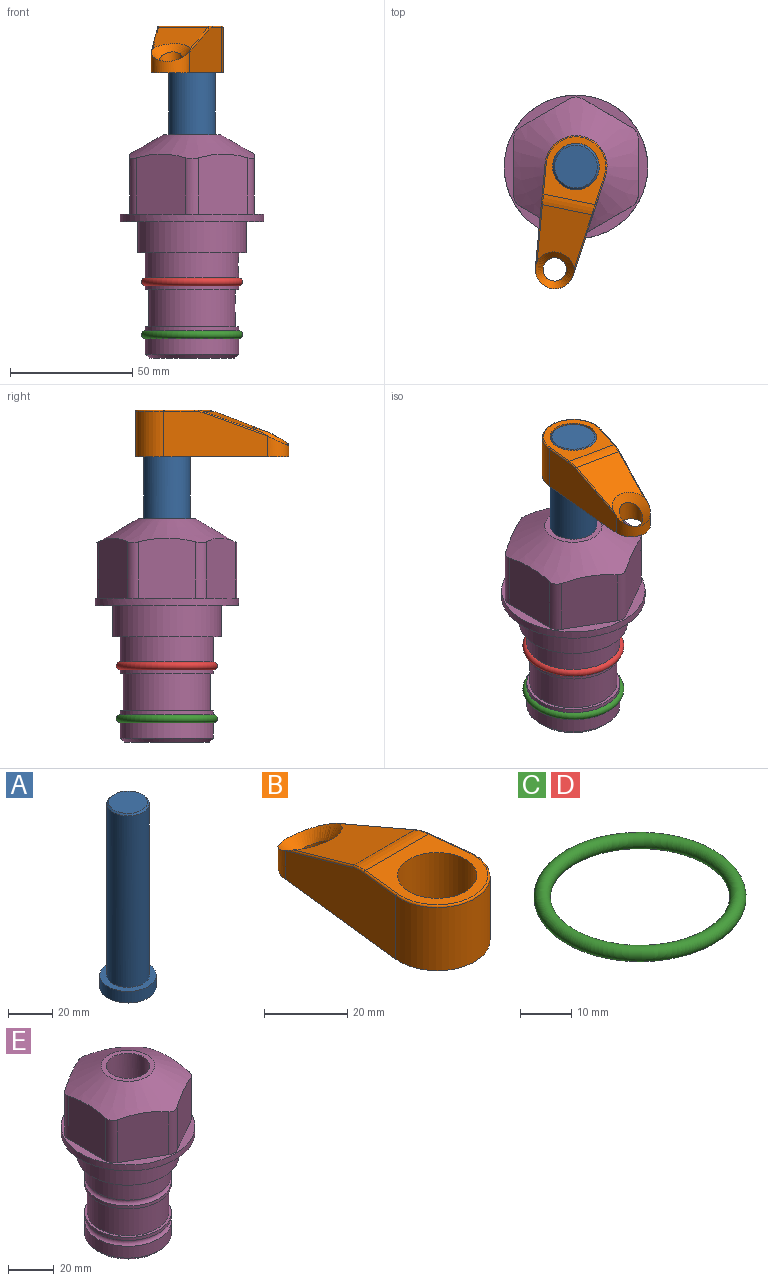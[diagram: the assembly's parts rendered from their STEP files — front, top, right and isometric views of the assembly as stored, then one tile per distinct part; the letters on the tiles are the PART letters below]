
ASSEMBLY  parts=5 mates=3
PART A: 6 faces, bbox 25.4x25.4x101.6 mm
  f0: plane 17.46x17.46mm, normal (0,0,1), area 239.5mm2, adj f5
  f1: plane 25.4x25.4mm, normal (0,0,-1), area 506.7mm2, adj f2
  f2: cylinder r=12.7mm len=25.4mm, axis (0,0,1), area 506.7mm2, adj f1,f3
  f3: plane 25.4x25.4mm, normal (0,0,1), area 221.7mm2, adj f2,f4
  f4: cylinder r=9.53mm len=94.46mm, axis (0,0,1), area 5653mm2, adj f3,f5
  f5: cone r=8.73mm half-angle=45deg, axis (0,0,-1), area 64.4mm2, adj f0,f4
PART B: 46 faces, bbox 27.5x66.1x19.1 mm
  f0: bspline ~0.38x0.18mm, area 0mm2, adj f5,f19,f45
  f1: plane 2.3x0.95mm, normal (0,0,-1), area 1mm2, adj f26,f31,f35
  f2: plane 63.5x25.4mm, normal (0,0,-1), area 561.7mm2, adj f3,f4,f5,f6,f7,f8,f20,f21
  f3: cylinder r=12.7mm len=25.4mm, axis (0,0,-1), area 792.2mm2, adj f2,f4,f6,f14
  f4: plane 42.33x18.54mm, normal (0.99,0.11,0), area 647mm2, adj f2,f3,f5,f12,f13,f15
  f5: cylinder r=7.94mm len=15.78mm, axis (0,0,-1), area 139.4mm2, adj f0,f2,f4,f6,f17,f45
  f6: plane 42.33x18.54mm, normal (-0.99,0.11,0), area 647mm2, adj f2,f3,f5,f16,f18,f19
  f7: cylinder r=9.53mm len=19.05mm, axis (0,0,-1), area 1140.1mm2, adj f2,f9
  f8: cylinder r=4.76mm len=9.53mm, axis (0,0,-1), area 163mm2, adj f2,f45
  f9: plane 25.83x24.38mm, normal (0,0,1), area 262.2mm2, adj f7,f11,f12,f14,f16
  f10: plane 22.98x20.56mm, normal (0,0.34,0.94), area 378mm2, adj f11,f15,f19,f45
  f11: cylinder r=12.7mm len=21.49mm, axis (-1,0,0), area 93.2mm2, adj f9,f10,f13,f18
  f12: cylinder r=0.51mm len=12.34mm, axis (0.11,-0.99,0), area 9.9mm2, adj f4,f9,f13,f14
  f13: bspline ~7.62x1.64mm, area 3.5mm2, adj f4,f11,f12,f15
  f14: torus R=12.19mm, axis (0,0,1), area 33.6mm2, adj f3,f9,f12,f16
  f15: cylinder r=0.51mm len=26.01mm, axis (0.1,-0.93,0.34), area 20.2mm2, adj f4,f10,f13,f17,f45
  f16: cylinder r=0.51mm len=12.34mm, axis (0.11,0.99,0), area 9.9mm2, adj f6,f9,f14,f18
  f17: bspline ~0.38x0.18mm, area 0mm2, adj f5,f15,f45
  f18: bspline ~7.62x1.64mm, area 3.5mm2, adj f6,f11,f16,f19
  f19: cylinder r=0.51mm len=26.01mm, axis (0.1,0.93,-0.34), area 20.2mm2, adj f0,f6,f10,f18,f45
  f20: plane 21.6x14.29mm, normal (-0.99,-0.11,0), area 242.6mm2, adj f2,f27,f29,f35,f37,f39
  f21: plane 21.6x14.29mm, normal (0.99,-0.11,0), area 242.6mm2, adj f2,f28,f30,f38,f40,f42
  f22: cylinder r=12.7mm len=14.29mm, axis (0,0,-1), area 173.4mm2, adj f2,f27,f28,f31,f32,f34
  f23: cylinder r=7.94mm len=7.28mm, axis (0,0,-1), area 52.1mm2, adj f2,f29,f30,f43
  f24: plane 2.3x0.95mm, normal (0,0,-1), area 1mm2, adj f26,f34,f38
  f25: plane 17.94x12.32mm, normal (0,-0.34,-0.94), area 191.2mm2, adj f26,f39,f42,f43
  f26: cylinder r=9.53mm len=12.93mm, axis (-1,0,0), area 37.5mm2, adj f1,f24,f25,f32,f37,f40
  f27: cylinder r=1.59mm len=14.29mm, axis (0,0,-1), area 49mm2, adj f2,f20,f22,f33
  f28: cylinder r=1.59mm len=14.29mm, axis (0,0,-1), area 49mm2, adj f2,f21,f22,f36
  f29: cylinder r=1.59mm len=7.28mm, axis (0,0,-1), area 22.1mm2, adj f2,f20,f23,f41
  f30: cylinder r=1.59mm len=7.28mm, axis (0,0,-1), area 22.1mm2, adj f2,f21,f23,f44
  f31: torus R=14.29mm, axis (0,0,1), area 5.8mm2, adj f1,f22,f32,f33
  f32: bspline ~11.06x2.73mm, area 20.8mm2, adj f22,f26,f31,f34
  f33: sphere r=1.59mm, area 5.4mm2, adj f27,f31,f35
  f34: torus R=14.29mm, axis (0,0,1), area 5.8mm2, adj f22,f24,f32,f36
  f35: cylinder r=1.59mm len=1.68mm, axis (-0.11,0.99,0), area 2.4mm2, adj f1,f20,f33,f37
  f36: sphere r=1.59mm, area 5.4mm2, adj f28,f34,f38
  f37: bspline ~5.82x2.33mm, area 7.7mm2, adj f20,f26,f35,f39
  f38: cylinder r=1.59mm len=1.68mm, axis (0.11,0.99,0), area 2.4mm2, adj f21,f24,f36,f40
  f39: cylinder r=1.59mm len=18.33mm, axis (0.1,-0.93,0.34), area 46.7mm2, adj f20,f25,f37,f41
  f40: bspline ~5.82x2.33mm, area 7.7mm2, adj f21,f26,f38,f42
  f41: sphere r=1.59mm, area 3.3mm2, adj f29,f39,f43
  f42: cylinder r=1.59mm len=18.33mm, axis (0.1,0.93,-0.34), area 46.7mm2, adj f21,f25,f40,f44
  f43: bspline ~8.31x1.84mm, area 15.3mm2, adj f23,f25,f41,f44
  f44: sphere r=1.59mm, area 3.3mm2, adj f30,f42,f43
  f45: bspline ~16.63x16.62mm, area 175.6mm2, adj f0,f5,f8,f10,f15,f17,f19
PART C: 1 faces, bbox 44.7x44.7x3.2 mm
  f0: torus R=19.05mm, axis (0,0,1), area 1193.9mm2
PART D: same geometry as C
PART E: 36 faces, bbox 58.7x58.7x91.2 mm
  f0: cylinder r=17.78mm len=35.56mm, axis (0,0,1), area 1670.8mm2, adj f23,f24,f31
  f1: cylinder r=19.05mm len=38.1mm, axis (0,0,1), area 1191.9mm2, adj f26,f27,f30
  f2: plane 58.66x58.66mm, normal (0,0,-1), area 1150.6mm2, adj f3,f28
  f3: cylinder r=29.33mm len=58.66mm, axis (0,0,-1), area 585.1mm2, adj f2,f4
  f4: plane 58.66x58.66mm, normal (0,0,1), area 475.9mm2, adj f3,f5,f6,f7,f8,f9,f10,f11
  f5: plane 24.5x20.32mm, normal (-0.5,0.87,0), area 562.8mm2, adj f4,f15,f16,f17
  f6: plane 24.5x20.32mm, normal (0.5,0.87,0), area 562.8mm2, adj f4,f14,f15,f17
  f7: plane 24.5x23.48mm, normal (1,0,0), area 562.8mm2, adj f4,f13,f14,f17
  f8: plane 24.5x20.32mm, normal (0.5,-0.87,0), area 562.8mm2, adj f4,f12,f13,f17
  f9: plane 24.5x20.32mm, normal (-0.5,-0.87,0), area 562.8mm2, adj f4,f11,f12,f17
  f10: plane 24.5x23.48mm, normal (-1,0,0), area 562.8mm2, adj f4,f11,f16,f17
  f11: cylinder r=5.08mm len=23.01mm, axis (0,0,-1), area 121.2mm2, adj f4,f9,f10,f17
  f12: cylinder r=5.08mm len=23.01mm, axis (0,0,-1), area 121.2mm2, adj f4,f8,f9,f17
  f13: cylinder r=5.08mm len=23.01mm, axis (0,0,-1), area 121.2mm2, adj f4,f7,f8,f17
  f14: cylinder r=5.08mm len=23.01mm, axis (0,0,-1), area 121.2mm2, adj f4,f6,f7,f17
  f15: cylinder r=5.08mm len=23.01mm, axis (0,0,-1), area 121.2mm2, adj f4,f5,f6,f17
  f16: cylinder r=5.08mm len=23.01mm, axis (0,0,-1), area 121.2mm2, adj f4,f5,f10,f17
  f17: cone r=11.73mm half-angle=60deg, axis (0,0,-1), area 2071.8mm2, adj f5,f6,f7,f8,f9,f10,f11,f12
  f18: plane 23.46x23.46mm, normal (0,0,1), area 147.4mm2, adj f17,f35
  f19: plane 34.93x34.93mm, normal (0,0,-1), area 958mm2, adj f29
  f20: cylinder r=19.05mm len=38.1mm, axis (0,0,1), area 760.1mm2, adj f21,f29
  f21: torus R=19.05mm, axis (0,0,1), area 565.3mm2, adj f20,f22
  f22: cylinder r=19.05mm len=38.1mm, axis (0,0,1), area 190mm2, adj f21,f23
  f23: plane 38.1x38.1mm, normal (0,0,1), area 146.9mm2, adj f0,f22
  f24: plane 38.1x38.1mm, normal (0,0,-1), area 146.9mm2, adj f0,f25
  f25: cylinder r=19.05mm len=38.1mm, axis (0,0,1), area 190mm2, adj f24,f26
  f26: torus R=19.05mm, axis (0,0,1), area 565.3mm2, adj f1,f25
  f27: plane 44.45x44.45mm, normal (0,0,-1), area 411.7mm2, adj f1,f28
  f28: cylinder r=22.23mm len=44.45mm, axis (0,0,1), area 1773.5mm2, adj f2,f27
  f29: cone r=19.05mm half-angle=45deg, axis (0,0,1), area 257.5mm2, adj f19,f20
  f30: cylinder r=3.17mm len=6.75mm, axis (-1,0,0), area 128mm2, adj f1,f33
  f31: cylinder r=3.17mm len=6.35mm, axis (-1,0,0), area 102.5mm2, adj f0,f33
  f32: plane 25.4x25.4mm, normal (0,0,1), area 506.7mm2, adj f33
  f33: cylinder r=12.7mm len=66.42mm, axis (0,0,-1), area 5236.2mm2, adj f30,f31,f32,f34
  f34: cone r=9.53mm half-angle=30deg, axis (0,0,-1), area 443.4mm2, adj f33,f35
  f35: cylinder r=9.53mm len=19.05mm, axis (0,0,-1), area 849mm2, adj f18,f34
PLACE A rot(axis=(0,0,-1),101.7deg) t=(0,0,6.38)mm
PLACE B rot(axis=(0,0,1),168.3deg) t=(0,0,60.99)mm
PLACE C t=(0,0,-21.59)mm
PLACE D at identity
PLACE E at identity fixed
MATE fastened C.f0 <-> E.f0  axis (0,0,1) through (0,0,-46.1)mm
MATE cylindrical A.f2 <-> E.f0  axis (0,0,1) through (0,0,32.01)mm
MATE fastened B.f3 <-> A.f2  axis (0,0,1) through (0,0,80.04)mm
